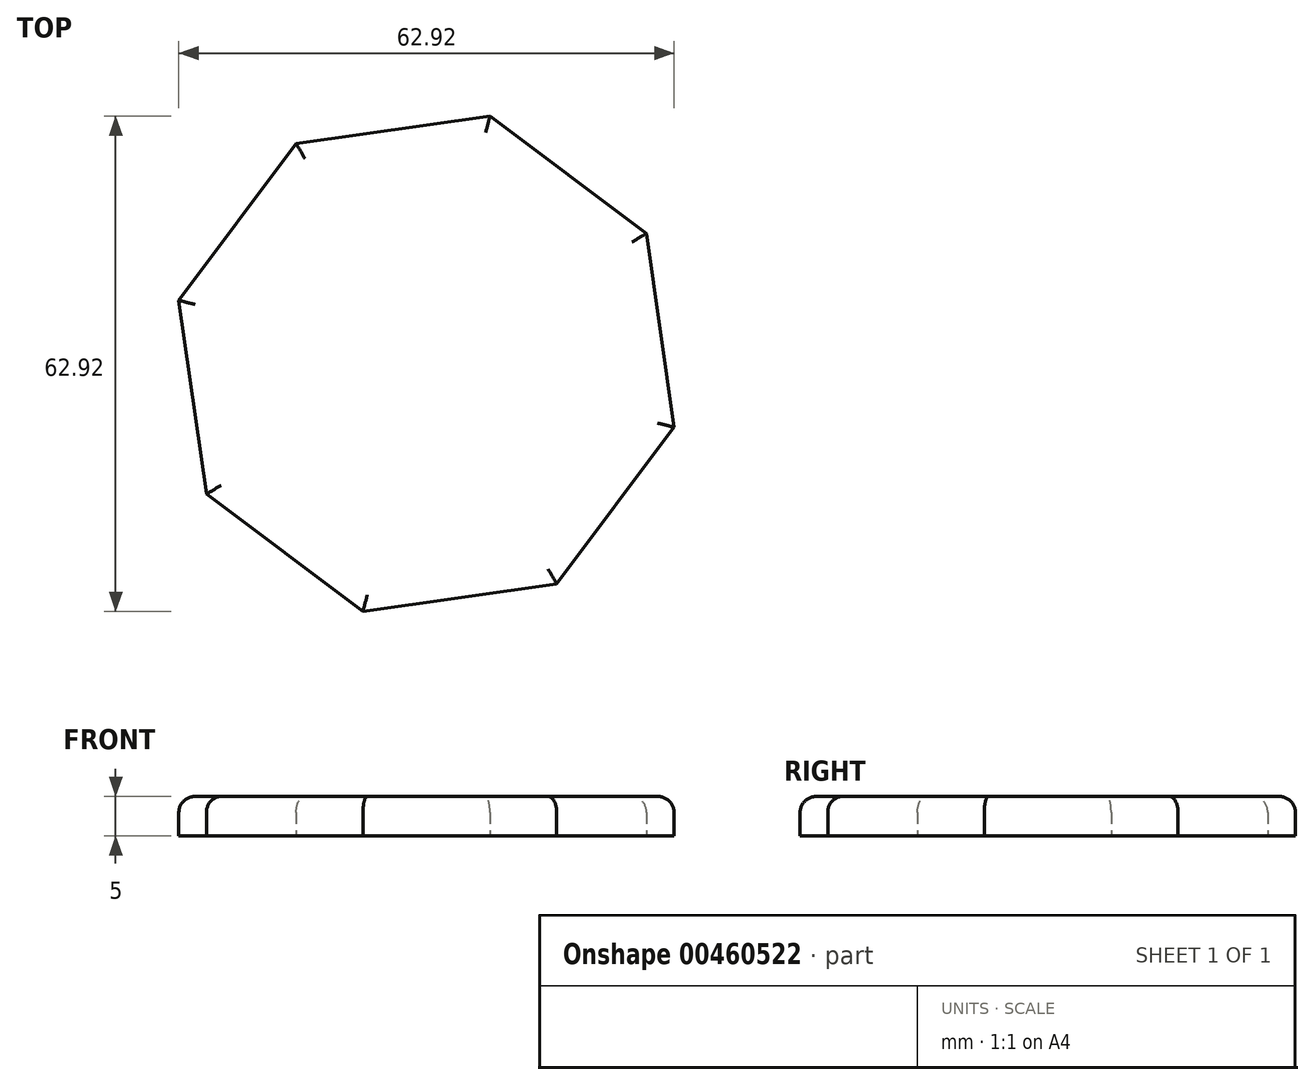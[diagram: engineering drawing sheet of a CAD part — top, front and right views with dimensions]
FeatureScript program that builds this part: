
annotation { "Feature Type Name" : "Feature", "Feature Type Description" : "" }
export const myFeature = defineFeature(function(context is Context, id is Id, definition is map)
    precondition{}
    {
        {
            var Q0;
            Q0=qCreatedBy(makeId("Top.planeOp"),FACE);
            var sketch = newSketch(context, id + "F0", { "sketchPlane" : qUnion([Q0])});
            skCircle(sketch, "E0.cCircle", {"center": v(0, 0) * mm, "radius": 30 * mm, "construction": true});
            skLineSegment(sketch, "E0.0", {"start": v(31.46, -8.06) * mm, "end": v(16.54, -27.94) * mm});
            skLineSegment(sketch, "E0.1", {"start": v(16.54, -27.94) * mm, "end": v(-8.06, -31.46) * mm});
            skLineSegment(sketch, "E0.2", {"start": v(-8.06, -31.46) * mm, "end": v(-27.94, -16.54) * mm});
            skLineSegment(sketch, "E0.3", {"start": v(-27.94, -16.54) * mm, "end": v(-31.46, 8.06) * mm});
            skLineSegment(sketch, "E0.4", {"start": v(-31.46, 8.06) * mm, "end": v(-16.54, 27.94) * mm});
            skLineSegment(sketch, "E0.5", {"start": v(-16.54, 27.94) * mm, "end": v(8.06, 31.46) * mm});
            skLineSegment(sketch, "E0.6", {"start": v(8.06, 31.46) * mm, "end": v(27.94, 16.54) * mm});
            skLineSegment(sketch, "E0.7", {"start": v(27.94, 16.54) * mm, "end": v(31.46, -8.06) * mm});
            skPoint(sketch, "E0.0.midPoint", {"position": v(24, -18) * mm});
            skSolve(sketch);
        }
        {
            var Q0;
            Q0 = qSketchRegion(id + "F0", true);
            extrude(context, id + "F1", {"entities" : qUnion([Q0]), "depth" : 5 * mm});
        }
        {
            var Q0;
            Q0=makeQuery(id+"F1.opExtrude","CAP_FACE",FACE,{"disambiguationData":[OSD([sQuery(id+"F0.wireOp",EDGE,"E0.0"),sQuery(id+"F0.wireOp",EDGE,"E0.1"),sQuery(id+"F0.wireOp",EDGE,"E0.2"),sQuery(id+"F0.wireOp",EDGE,"E0.3"),sQuery(id+"F0.wireOp",EDGE,"E0.4"),sQuery(id+"F0.wireOp",EDGE,"E0.5"),sQuery(id+"F0.wireOp",EDGE,"E0.6"),sQuery(id+"F0.wireOp",EDGE,"E0.7")])],"isStart":false});
            fillet(context, id + "F2", {"entities" : qUnion([Q0]), "radius" : 2 * mm, "tangentPropagation" : true, "allowEdgeOverflow" : false});
        }
    });
